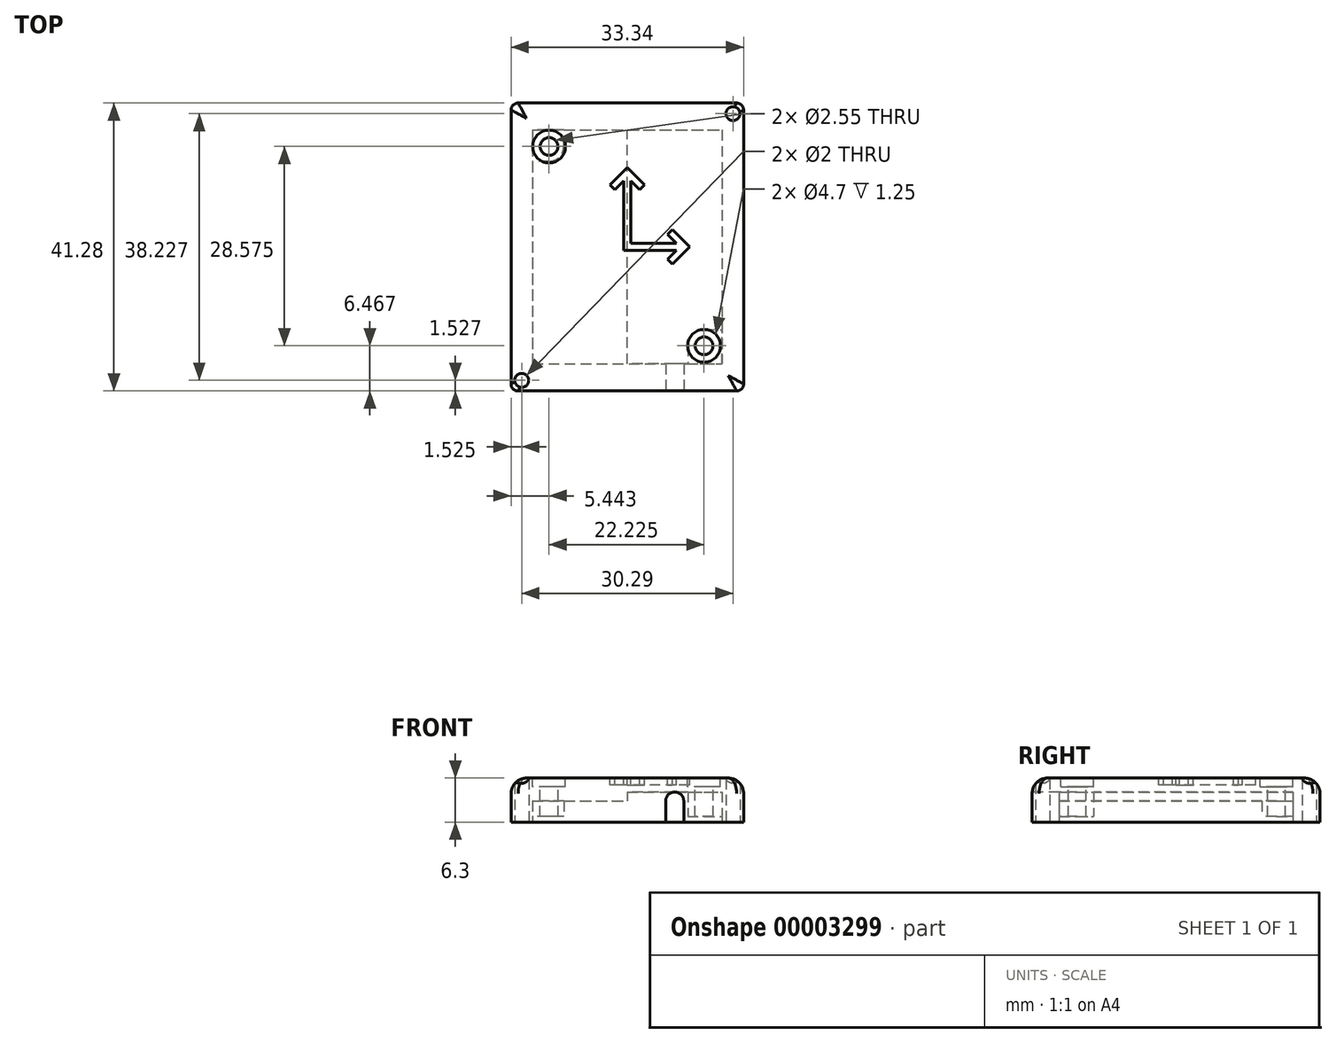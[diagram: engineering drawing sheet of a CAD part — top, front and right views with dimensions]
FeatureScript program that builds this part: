
annotation { "Feature Type Name" : "Feature", "Feature Type Description" : "" }
export const myFeature = defineFeature(function(context is Context, id is Id, definition is map)
    precondition{}
    {
        {
            var Q0;
            Q0=qCreatedBy(makeId("Top.planeOp"),FACE);
            var sketch = newSketch(context, id + "F0", { "sketchPlane" : qUnion([Q0])});
            skLineSegment(sketch, "E0.rect.bottom", {"start": v(16.67, 20.64) * mm, "end": v(-16.67, 20.64) * mm});
            skLineSegment(sketch, "E0.rect.top", {"start": v(16.67, -20.64) * mm, "end": v(-16.67, -20.64) * mm});
            skLineSegment(sketch, "E0.rect.left", {"start": v(16.67, 20.64) * mm, "end": v(16.67, -20.64) * mm});
            skLineSegment(sketch, "E0.rect.right", {"start": v(-16.67, 20.64) * mm, "end": v(-16.67, -20.64) * mm});
            skPoint(sketch, "E0.rect.middle", {"position": v(0, 0) * mm});
            skSolve(sketch);
        }
        {
            var Q0;
            Q0=qSketchRegion(id+"F0",true);
            extrude(context, id + "F1", {"entities" : qUnion([Q0]), "oppositeDirection" : true, "depth" : 5 * mm});
        }
        {
            var Q0;
            Q0=makeQuery(id+"F1.opExtrude","CAP_FACE",FACE,{"disambiguationData":[OSD([sQuery(id+"F0.wireOp",EDGE,"E0.rect.bottom"),sQuery(id+"F0.wireOp",EDGE,"E0.rect.top"),sQuery(id+"F0.wireOp",EDGE,"E0.rect.left"),sQuery(id+"F0.wireOp",EDGE,"E0.rect.right")])],"isStart":true});
            var sketch = newSketch(context, id + "F2", { "sketchPlane" : qUnion([Q0])});
            skLineSegment(sketch, "E1.rect.bottom", {"start": v(13.33, 16.51) * mm, "end": v(-13.34, 16.51) * mm});
            skLineSegment(sketch, "E1.rect.top", {"start": v(13.34, -16.51) * mm, "end": v(-13.33, -16.51) * mm});
            skLineSegment(sketch, "E1.rect.left", {"start": v(13.33, 16.51) * mm, "end": v(13.34, -16.51) * mm});
            skLineSegment(sketch, "E1.rect.right", {"start": v(-13.34, 16.51) * mm, "end": v(-13.33, -16.51) * mm});
            skPoint(sketch, "E1.rect.middle", {"position": v(0, 0) * mm});
            skCircle(sketch, "E2", {"center": v(11.23, 14.4) * mm, "radius": 1.25 * mm});
            skCircle(sketch, "E3", {"center": v(-11, -14.17) * mm, "radius": 1.25 * mm});
            skCircle(sketch, "E4", {"center": v(11.23, 14.4) * mm, "radius": 2.1 * mm});
            skCircle(sketch, "E5", {"center": v(-11, -14.17) * mm, "radius": 2.34 * mm});
            skLineSegment(sketch, "E6.0", {"start": v(13.59, 16.76) * mm, "end": v(-13.59, 16.76) * mm});
            skLineSegment(sketch, "E6.1", {"start": v(13.59, 16.76) * mm, "end": v(13.59, -16.76) * mm});
            skLineSegment(sketch, "E6.2", {"start": v(13.59, -16.76) * mm, "end": v(-13.59, -16.76) * mm});
            skLineSegment(sketch, "E6.3", {"start": v(-13.59, 16.76) * mm, "end": v(-13.59, -16.76) * mm});
            skLineSegment(sketch, "E7", {"start": v(9.12, 14.4) * mm, "end": v(9.12, 16.76) * mm});
            skLineSegment(sketch, "E8", {"start": v(11.23, 12.3) * mm, "end": v(13.59, 12.3) * mm});
            skLineSegment(sketch, "E9", {"start": v(-11, -11.84) * mm, "end": v(-13.59, -11.84) * mm});
            skLineSegment(sketch, "E10", {"start": v(-8.66, -14.17) * mm, "end": v(-8.66, -16.76) * mm});
            skSolve(sketch);
        }
        {
            var Q0;
            {var subQ6=sQuery(id+"F2.wireOp",EDGE,"E1.rect.right");var subQ10=sQuery(id+"F2.wireOp",EDGE,"E1.rect.bottom");var subQ18=makeQuery(id+"F2.imprint","INTERSECT",VERTEX,{"derivedFrom":[subQ10,subQ6]});Q0=makeQuery(id+"F2.imprint","IMPRINT",FACE,{"disambiguationData":[TD([[makeQuery(id+"F2.imprint","IMPRINT",EDGE,{"disambiguationData":[TD([[subQ18,1.0]])],"derivedFrom":subQ10}),1.0]])]});}
            var Q1;
            {var subQ1=sQuery(id+"F2.wireOp",EDGE,"E1.rect.right");var subQ6=sQuery(id+"F2.wireOp",EDGE,"E1.rect.bottom");var subQ11=makeQuery(id+"F2.imprint","INTERSECT",VERTEX,{"derivedFrom":[subQ6,subQ1]});Q1=makeQuery(id+"F2.imprint","IMPRINT",FACE,{"disambiguationData":[TD([[makeQuery(id+"F2.imprint","IMPRINT",EDGE,{"disambiguationData":[TD([[subQ11,1.0]])],"derivedFrom":subQ6}),-1.0]])]});}
            var Q2;
            {var subQ1=sQuery(id+"F2.wireOp",EDGE,"E1.rect.left");var subQ6=sQuery(id+"F2.wireOp",EDGE,"E1.rect.top");var subQ11=makeQuery(id+"F2.imprint","INTERSECT",VERTEX,{"derivedFrom":[subQ6,subQ1]});Q2=makeQuery(id+"F2.imprint","IMPRINT",FACE,{"disambiguationData":[TD([[makeQuery(id+"F2.imprint","IMPRINT",EDGE,{"disambiguationData":[TD([[subQ11,-1.0]])],"derivedFrom":subQ6}),1.0]])]});}
            extrude(context, id + "F3", {"entities" : qUnion([Q0, Q1, Q2]), "operationType" : NewBodyOperationType.REMOVE, "oppositeDirection" : true, "depth" : 3 * mm});
        }
        {
            var Q0;
            Q0=makeQuery(id+"F1.opExtrude","CAP_FACE",FACE,{"disambiguationData":[OSD([sQuery(id+"F0.wireOp",EDGE,"E0.rect.bottom"),sQuery(id+"F0.wireOp",EDGE,"E0.rect.top"),sQuery(id+"F0.wireOp",EDGE,"E0.rect.left"),sQuery(id+"F0.wireOp",EDGE,"E0.rect.right")])],"isStart":true});
            var sketch = newSketch(context, id + "F4", { "sketchPlane" : qUnion([Q0])});
            skLineSegment(sketch, "E11", {"start": v(9.12, 16.76) * mm, "end": v(13.59, 16.76) * mm});
            skLineSegment(sketch, "E12", {"start": v(13.59, 16.76) * mm, "end": v(13.59, 12.3) * mm});
            skLineSegment(sketch, "E13", {"start": v(13.59, 12.3) * mm, "end": v(11.23, 12.3) * mm});
            skArc(sketch, "E14", {"start": v(9.12, 14.4) * mm, "mid": v(9.74, 12.91) * mm, "end": v(11.23, 12.3) * mm});
            skLineSegment(sketch, "E15", {"start": v(9.12, 14.4) * mm, "end": v(9.12, 16.76) * mm});
            skArc(sketch, "E16", {"start": v(-8.66, -14.17) * mm, "mid": v(-9.35, -12.52) * mm, "end": v(-11, -11.84) * mm});
            skLineSegment(sketch, "E17", {"start": v(-8.66, -14.17) * mm, "end": v(-8.66, -16.76) * mm});
            skLineSegment(sketch, "E18", {"start": v(-8.66, -16.76) * mm, "end": v(-13.59, -16.76) * mm});
            skLineSegment(sketch, "E19", {"start": v(-13.59, -16.76) * mm, "end": v(-13.59, -11.84) * mm});
            skLineSegment(sketch, "E20", {"start": v(-13.59, -11.84) * mm, "end": v(-11, -11.84) * mm});
            skSolve(sketch);
        }
        {
            var Q0;
            Q0=qSketchRegion(id+"F4",true);
            extrude(context, id + "F5", {"entities" : qUnion([Q0]), "operationType" : NewBodyOperationType.REMOVE, "oppositeDirection" : true, "depth" : .8 * mm});
        }
        {
            var Q0;
            Q0=makeQuery(id+"F5.boolean.opBoolean","COPY",FACE,{"derivedFrom":makeQuery(id+"F5.opExtrude","CAP_FACE",FACE,{"disambiguationData":[OSD([sQuery(id+"F4.wireOp",EDGE,"E11"),sQuery(id+"F4.wireOp",EDGE,"E12"),sQuery(id+"F4.wireOp",EDGE,"E13"),sQuery(id+"F4.wireOp",EDGE,"E14"),sQuery(id+"F4.wireOp",EDGE,"E15")])],"isStart":false})});
            var sketch = newSketch(context, id + "F6", { "sketchPlane" : qUnion([Q0])});
            skCircle(sketch, "E21", {"center": v(11.23, 14.4) * mm, "radius": 1.02 * mm});
            skSolve(sketch);
        }
        {
            var Q0;
            Q0=qSketchRegion(id+"F6",true);
            extrude(context, id + "F7", {"entities" : qUnion([Q0]), "operationType" : NewBodyOperationType.REMOVE, "oppositeDirection" : true, "depth" : 25.4 * mm});
        }
        {
            var Q0;
            Q0=makeQuery(id+"F5.boolean.opBoolean","COPY",FACE,{"derivedFrom":makeQuery(id+"F5.opExtrude","CAP_FACE",FACE,{"disambiguationData":[OSD([sQuery(id+"F4.wireOp",EDGE,"E16"),sQuery(id+"F4.wireOp",EDGE,"E17"),sQuery(id+"F4.wireOp",EDGE,"E18"),sQuery(id+"F4.wireOp",EDGE,"E19"),sQuery(id+"F4.wireOp",EDGE,"E20")])],"isStart":false})});
            var sketch = newSketch(context, id + "F8", { "sketchPlane" : qUnion([Q0])});
            skCircle(sketch, "E22", {"center": v(-11, -14.17) * mm, "radius": 1.02 * mm});
            skSolve(sketch);
        }
        {
            var Q0;
            Q0=qSketchRegion(id+"F8",true);
            extrude(context, id + "F9", {"entities" : qUnion([Q0]), "operationType" : NewBodyOperationType.REMOVE, "oppositeDirection" : true, "depth" : 25.4 * mm});
        }
        {
            var Q0;
            Q0=makeQuery(id+"F1.opExtrude","CAP_FACE",FACE,{"disambiguationData":[OSD([sQuery(id+"F0.wireOp",EDGE,"E0.rect.bottom"),sQuery(id+"F0.wireOp",EDGE,"E0.rect.top"),sQuery(id+"F0.wireOp",EDGE,"E0.rect.left"),sQuery(id+"F0.wireOp",EDGE,"E0.rect.right")])],"isStart":true});
            var sketch = newSketch(context, id + "F10", { "sketchPlane" : qUnion([Q0])});
            skLineSegment(sketch, "E23.bottom", {"start": v(-13.59, 16.76) * mm, "end": v(-5.09, 16.76) * mm});
            skLineSegment(sketch, "E23.top", {"start": v(-13.59, 20.64) * mm, "end": v(-5.09, 20.64) * mm});
            skLineSegment(sketch, "E23.left", {"start": v(-13.59, 16.76) * mm, "end": v(-13.59, 20.64) * mm});
            skLineSegment(sketch, "E23.right", {"start": v(-5.09, 16.76) * mm, "end": v(-5.09, 20.64) * mm});
            skLineSegment(sketch, "E24.bottom", {"start": v(13.59, -16.76) * mm, "end": v(4.59, -16.76) * mm});
            skLineSegment(sketch, "E24.top", {"start": v(13.59, -20.64) * mm, "end": v(4.59, -20.64) * mm});
            skLineSegment(sketch, "E24.left", {"start": v(13.59, -16.76) * mm, "end": v(13.59, -20.64) * mm});
            skLineSegment(sketch, "E24.right", {"start": v(4.59, -16.76) * mm, "end": v(4.59, -20.64) * mm});
            skSolve(sketch);
        }
        {
            var Q0;
            Q0=qSketchRegion(id+"F10",true);
            extrude(context, id + "F11", {"entities" : qUnion([Q0]), "operationType" : NewBodyOperationType.REMOVE, "oppositeDirection" : true, "depth" : .4 * mm});
        }
        {
            var Q0;
            {var subQ0=sQuery(id+"F0.wireOp",EDGE,"E0.rect.bottom");var subQ1=sQuery(id+"F0.wireOp",EDGE,"E0.rect.top");var subQ2=sQuery(id+"F0.wireOp",EDGE,"E0.rect.right");Q0=makeQuery(id+"F11.boolean.opBoolean","SPLIT",FACE,{"disambiguationData":[TD([makeQuery(id+"F1.opExtrude","SWEPT_FACE",FACE,{"disambiguationData":[OSD([subQ2])]})])],"derivedFrom":makeQuery(id+"F1.opExtrude","CAP_FACE",FACE,{"disambiguationData":[OSD([subQ0,subQ1,sQuery(id+"F0.wireOp",EDGE,"E0.rect.left"),subQ2])],"isStart":true})});}
            var sketch = newSketch(context, id + "F12", { "sketchPlane" : qUnion([Q0])});
            skCircle(sketch, "E25", {"center": v(-15.14, 19.11) * mm, "radius": 1 * mm});
            skSolve(sketch);
        }
        {
            var Q0;
            Q0=qSketchRegion(id+"F12",true);
            extrude(context, id + "F13", {"entities" : qUnion([Q0]), "operationType" : NewBodyOperationType.ADD, "depth" : 3.5 * mm});
        }
        {
            var Q0;
            {var subQ0=sQuery(id+"F0.wireOp",EDGE,"E0.rect.bottom");var subQ1=sQuery(id+"F0.wireOp",EDGE,"E0.rect.top");var subQ2=sQuery(id+"F0.wireOp",EDGE,"E0.rect.left");Q0=makeQuery(id+"F11.boolean.opBoolean","SPLIT",FACE,{"disambiguationData":[TD([makeQuery(id+"F1.opExtrude","SWEPT_FACE",FACE,{"disambiguationData":[OSD([subQ2])]})])],"derivedFrom":makeQuery(id+"F1.opExtrude","CAP_FACE",FACE,{"disambiguationData":[OSD([subQ0,subQ1,subQ2,sQuery(id+"F0.wireOp",EDGE,"E0.rect.right")])],"isStart":true})});}
            var sketch = newSketch(context, id + "F14", { "sketchPlane" : qUnion([Q0])});
            skCircle(sketch, "E26", {"center": v(15.14, -19.11) * mm, "radius": 1 * mm});
            skSolve(sketch);
        }
        {
            var Q0;
            Q0=qSketchRegion(id+"F14",true);
            extrude(context, id + "F15", {"entities" : qUnion([Q0]), "operationType" : NewBodyOperationType.ADD, "depth" : 3.5 * mm});
        }
        {
            var Q0;
            Q0=makeQuery(id+"F13.opExtrude","CAP_EDGE",EDGE,{"disambiguationData":[OSD([sQuery(id+"F12.wireOp",EDGE,"E25")])],"isStart":false});
            var Q1;
            Q1=makeQuery(id+"F15.opExtrude","CAP_EDGE",EDGE,{"disambiguationData":[OSD([sQuery(id+"F14.wireOp",EDGE,"E26")])],"isStart":false});
            fillet(context, id + "F16", {"entities" : qUnion([Q0, Q1]), "radius" : 1 * mm, "tangentPropagation" : true, "allowEdgeOverflow" : false});
        }
        {
            var Q0;
            Q0=makeQuery(id+"F1.opExtrude","SWEPT_EDGE",EDGE,{"disambiguationData":[OSD([sQuery(id+"F0.wireOp",EDGE,"E0.rect.bottom"),sQuery(id+"F0.wireOp",EDGE,"E0.rect.left")])]});
            var Q1;
            Q1=makeQuery(id+"F1.opExtrude","SWEPT_EDGE",EDGE,{"disambiguationData":[OSD([sQuery(id+"F0.wireOp",EDGE,"E0.rect.top"),sQuery(id+"F0.wireOp",EDGE,"E0.rect.left")])]});
            var Q2;
            Q2=makeQuery(id+"F1.opExtrude","SWEPT_EDGE",EDGE,{"disambiguationData":[OSD([sQuery(id+"F0.wireOp",EDGE,"E0.rect.top"),sQuery(id+"F0.wireOp",EDGE,"E0.rect.right")])]});
            var Q3;
            Q3=makeQuery(id+"F1.opExtrude","SWEPT_EDGE",EDGE,{"disambiguationData":[OSD([sQuery(id+"F0.wireOp",EDGE,"E0.rect.bottom"),sQuery(id+"F0.wireOp",EDGE,"E0.rect.right")])]});
            var Q4;
            Q4=makeQuery(id+"F1.opExtrude","CAP_EDGE",EDGE,{"disambiguationData":[OSD([sQuery(id+"F0.wireOp",EDGE,"E0.rect.top")])],"isStart":false});
            var Q5;
            Q5=makeQuery(id+"F1.opExtrude","CAP_EDGE",EDGE,{"disambiguationData":[OSD([sQuery(id+"F0.wireOp",EDGE,"E0.rect.left")])],"isStart":false});
            var Q6;
            Q6=makeQuery(id+"F1.opExtrude","CAP_EDGE",EDGE,{"disambiguationData":[OSD([sQuery(id+"F0.wireOp",EDGE,"E0.rect.bottom")])],"isStart":false});
            var Q7;
            Q7=makeQuery(id+"F1.opExtrude","CAP_EDGE",EDGE,{"disambiguationData":[OSD([sQuery(id+"F0.wireOp",EDGE,"E0.rect.right")])],"isStart":false});
            fillet(context, id + "F17", {"entities" : qUnion([Q0, Q1, Q2, Q3, Q4, Q5, Q6, Q7]), "radius" : 1 * mm, "tangentPropagation" : true, "allowEdgeOverflow" : false});
        }
        {
            var Q0;
            Q0=makeQuery(id+"F11.boolean.opBoolean","COPY",FACE,{"derivedFrom":makeQuery(id+"F11.opExtrude","CAP_FACE",FACE,{"disambiguationData":[OSD([sQuery(id+"F10.wireOp",EDGE,"E24.bottom"),sQuery(id+"F10.wireOp",EDGE,"E24.top"),sQuery(id+"F10.wireOp",EDGE,"E24.left"),sQuery(id+"F10.wireOp",EDGE,"E24.right")])],"isStart":false})});
            var sketch = newSketch(context, id + "F18", { "sketchPlane" : qUnion([Q0])});
            skLineSegment(sketch, "E27.bottom", {"start": v(4.59, -16.76) * mm, "end": v(13.59, -16.76) * mm});
            skLineSegment(sketch, "E27.top", {"start": v(4.59, -20.64) * mm, "end": v(13.59, -20.64) * mm});
            skLineSegment(sketch, "E27.left", {"start": v(4.59, -16.76) * mm, "end": v(4.59, -20.64) * mm});
            skLineSegment(sketch, "E27.right", {"start": v(13.59, -16.76) * mm, "end": v(13.59, -20.64) * mm});
            skSolve(sketch);
        }
        {
            var Q0;
            Q0=qSketchRegion(id+"F18",true);
            extrude(context, id + "F19", {"entities" : qUnion([Q0]), "operationType" : NewBodyOperationType.ADD, "depth" : .4 * mm});
        }
        {
            var Q0;
            Q0=makeQuery(id+"F11.boolean.opBoolean","COPY",FACE,{"derivedFrom":makeQuery(id+"F11.opExtrude","CAP_FACE",FACE,{"disambiguationData":[OSD([sQuery(id+"F10.wireOp",EDGE,"E23.bottom"),sQuery(id+"F10.wireOp",EDGE,"E23.top"),sQuery(id+"F10.wireOp",EDGE,"E23.left"),sQuery(id+"F10.wireOp",EDGE,"E23.right")])],"isStart":false})});
            var sketch = newSketch(context, id + "F20", { "sketchPlane" : qUnion([Q0])});
            skLineSegment(sketch, "E28.bottom", {"start": v(-13.59, 20.64) * mm, "end": v(-5.09, 20.64) * mm});
            skLineSegment(sketch, "E28.top", {"start": v(-13.59, 16.76) * mm, "end": v(-5.09, 16.76) * mm});
            skLineSegment(sketch, "E28.left", {"start": v(-13.59, 20.64) * mm, "end": v(-13.59, 16.76) * mm});
            skLineSegment(sketch, "E28.right", {"start": v(-5.09, 20.64) * mm, "end": v(-5.09, 16.76) * mm});
            skSolve(sketch);
        }
        {
            var Q0;
            Q0=qSketchRegion(id+"F20",true);
            extrude(context, id + "F21", {"entities" : qUnion([Q0]), "operationType" : NewBodyOperationType.ADD, "depth" : .4 * mm});
        }
        {
            var Q0;
            Q0=qCreatedBy(makeId("Top.planeOp"),FACE);
            var sketch = newSketch(context, id + "F22", { "sketchPlane" : qUnion([Q0])});
            skLineSegment(sketch, "E29", {"start": v(0, 0) * mm, "end": v(0, 40.72) * mm});
            skSolve(sketch);
        }
        {
            var Q0;
            Q0=makeQuery(id+"F1.opExtrude","SWEPT_BODY",BODY,{"disambiguationData":[OSD([sQuery(id+"F0.wireOp",EDGE,"E0.rect.bottom"),sQuery(id+"F0.wireOp",EDGE,"E0.rect.top"),sQuery(id+"F0.wireOp",EDGE,"E0.rect.left"),sQuery(id+"F0.wireOp",EDGE,"E0.rect.right")])]});
            var Q1;
            Q1=sQuery(id+"F22.wireOp",EDGE,"E29");
            transform(context, id + "F23", {"entities" : qUnion([Q0]), "transformType" : TransformType.ROTATION, "transformAxis" : qUnion([Q1]), "angle" : 180 * degree, "makeCopy" : false});
        }
        {
            var Q0;
            Q0=makeQuery(id+"F1.opExtrude","SWEPT_BODY",BODY,{"disambiguationData":[OSD([sQuery(id+"F0.wireOp",EDGE,"E0.rect.bottom"),sQuery(id+"F0.wireOp",EDGE,"E0.rect.top"),sQuery(id+"F0.wireOp",EDGE,"E0.rect.left"),sQuery(id+"F0.wireOp",EDGE,"E0.rect.right")])]});
            var Q1;
            Q1=qCreatedBy(makeId("Top.planeOp"),FACE);
            mirror(context, id + "F24", {"entities" : qUnion([Q0]), "mirrorPlane" : qUnion([Q1])});
        }
        {
            var Q0;
            Q0=makeQuery(id+"F1.opExtrude","SWEPT_BODY",BODY,{"disambiguationData":[OSD([sQuery(id+"F0.wireOp",EDGE,"E0.rect.bottom"),sQuery(id+"F0.wireOp",EDGE,"E0.rect.top"),sQuery(id+"F0.wireOp",EDGE,"E0.rect.left"),sQuery(id+"F0.wireOp",EDGE,"E0.rect.right")])]});
            deleteBodies(context, id + "F25", {"entities" : qUnion([Q0])});
        }
        {
            var Q0;
            Q0=makeQuery(id+"F24.opPattern","COPY",BODY,{"derivedFrom":makeQuery(id+"F1.opExtrude","SWEPT_BODY",BODY,{"disambiguationData":[OSD([sQuery(id+"F0.wireOp",EDGE,"E0.rect.bottom"),sQuery(id+"F0.wireOp",EDGE,"E0.rect.top"),sQuery(id+"F0.wireOp",EDGE,"E0.rect.left"),sQuery(id+"F0.wireOp",EDGE,"E0.rect.right")])]}),"instanceName":"1"});
            var Q1;
            Q1=qCreatedBy(makeId("Top.planeOp"),FACE);
            mirror(context, id + "F26", {"entities" : qUnion([Q0]), "mirrorPlane" : qUnion([Q1])});
        }
        {
            var Q0;
            Q0=makeQuery(id+"F24.opPattern","COPY",BODY,{"derivedFrom":makeQuery(id+"F1.opExtrude","SWEPT_BODY",BODY,{"disambiguationData":[OSD([sQuery(id+"F0.wireOp",EDGE,"E0.rect.bottom"),sQuery(id+"F0.wireOp",EDGE,"E0.rect.top"),sQuery(id+"F0.wireOp",EDGE,"E0.rect.left"),sQuery(id+"F0.wireOp",EDGE,"E0.rect.right")])]}),"instanceName":"1"});
            deleteBodies(context, id + "F27", {"entities" : qUnion([Q0])});
        }
        {
            var Q0;
            {var subQ0=sQuery(id+"F0.wireOp",EDGE,"E0.rect.bottom");var subQ1=sQuery(id+"F0.wireOp",EDGE,"E0.rect.top");var subQ2=sQuery(id+"F0.wireOp",EDGE,"E0.rect.left");var subQ3=sQuery(id+"F0.wireOp",EDGE,"E0.rect.right");var subQ4=makeQuery(id+"F1.opExtrude","CAP_FACE",FACE,{"disambiguationData":[OSD([subQ0,subQ1,subQ2,subQ3])],"isStart":true});Q0=makeQuery(id+"F26.opPattern","COPY",FACE,{"derivedFrom":makeQuery(id+"F24.opPattern","COPY",FACE,{"derivedFrom":makeQuery(id+"F21.boolean.opBoolean","MERGE",FACE,{"derivedFrom":[makeQuery(id+"F19.boolean.opBoolean","MERGE",FACE,{"derivedFrom":[makeQuery(id+"F11.boolean.opBoolean","SPLIT",FACE,{"disambiguationData":[TD([makeQuery(id+"F1.opExtrude","SWEPT_FACE",FACE,{"disambiguationData":[OSD([subQ3])]})])],"derivedFrom":subQ4}),makeQuery(id+"F11.boolean.opBoolean","SPLIT",FACE,{"disambiguationData":[TD([makeQuery(id+"F1.opExtrude","SWEPT_FACE",FACE,{"disambiguationData":[OSD([subQ2])]})])],"derivedFrom":subQ4}),makeQuery(id+"F19.opExtrude","CAP_FACE",FACE,{"disambiguationData":[OSD([sQuery(id+"F18.wireOp",EDGE,"E27.bottom"),sQuery(id+"F18.wireOp",EDGE,"E27.top"),sQuery(id+"F18.wireOp",EDGE,"E27.left"),sQuery(id+"F18.wireOp",EDGE,"E27.right")])],"isStart":false})]}),makeQuery(id+"F21.opExtrude","CAP_FACE",FACE,{"disambiguationData":[OSD([sQuery(id+"F20.wireOp",EDGE,"E28.bottom"),sQuery(id+"F20.wireOp",EDGE,"E28.top"),sQuery(id+"F20.wireOp",EDGE,"E28.left"),sQuery(id+"F20.wireOp",EDGE,"E28.right")])],"isStart":false})]}),"instanceName":"1"}),"instanceName":"1"});}
            var sketch = newSketch(context, id + "F28", { "sketchPlane" : qUnion([Q0])});
            skCircle(sketch, "E30", {"center": v(-15.14, 19.11) * mm, "radius": 1 * mm});
            skPoint(sketch, "E30.first.point", {"position": v(-15.31, 18.13) * mm});
            skPoint(sketch, "E30.second.point", {"position": v(-14.3, 19.64) * mm});
            skPoint(sketch, "E30.third.point", {"position": v(-15.62, 20) * mm});
            skCircle(sketch, "E31", {"center": v(15.14, -19.11) * mm, "radius": 1 * mm});
            skPoint(sketch, "E31.first.point", {"position": v(15.27, -18.12) * mm});
            skPoint(sketch, "E31.second.point", {"position": v(14.16, -19.27) * mm});
            skPoint(sketch, "E31.third.point", {"position": v(15.62, -20) * mm});
            skSolve(sketch);
        }
        {
            var Q0;
            Q0 = qSketchRegion(id + "F28", true);
            extrude(context, id + "F29", {"entities" : qUnion([Q0]), "operationType" : NewBodyOperationType.REMOVE, "endBound" : BoundingType.SYMMETRIC, "oppositeDirection" : true, "depth" : 25.4 * mm});
        }
        {
            var Q0;
            Q0=makeQuery(id+"F26.opPattern","COPY",FACE,{"derivedFrom":makeQuery(id+"F24.opPattern","COPY",FACE,{"derivedFrom":makeQuery(id+"F3.boolean.opBoolean","COPY",FACE,{"derivedFrom":makeQuery(id+"F3.opExtrude","CAP_FACE",FACE,{"disambiguationData":[OSD([sQuery(id+"F2.wireOp",EDGE,"E4"),sQuery(id+"F2.wireOp",EDGE,"E5"),sQuery(id+"F2.wireOp",EDGE,"E6.0"),sQuery(id+"F2.wireOp",EDGE,"E6.1"),sQuery(id+"F2.wireOp",EDGE,"E6.2"),sQuery(id+"F2.wireOp",EDGE,"E6.3"),sQuery(id+"F2.wireOp",EDGE,"E7"),sQuery(id+"F2.wireOp",EDGE,"E8"),sQuery(id+"F2.wireOp",EDGE,"E9"),sQuery(id+"F2.wireOp",EDGE,"E10")])],"isStart":false})}),"instanceName":"1"}),"instanceName":"1"});
            var sketch = newSketch(context, id + "F30", { "sketchPlane" : qUnion([Q0])});
            skLineSegment(sketch, "E32.rect.bottom", {"start": v(-16.67, 20.64) * mm, "end": v(16.67, 20.64) * mm});
            skLineSegment(sketch, "E32.rect.top", {"start": v(-16.67, -20.64) * mm, "end": v(16.67, -20.64) * mm});
            skLineSegment(sketch, "E32.rect.left", {"start": v(-16.67, 20.64) * mm, "end": v(-16.67, -20.64) * mm});
            skLineSegment(sketch, "E32.rect.right", {"start": v(16.67, 20.64) * mm, "end": v(16.67, -20.64) * mm});
            skPoint(sketch, "E32.rect.middle", {"position": v(0, 0) * mm});
            skCircle(sketch, "E33", {"center": v(-15.14, 19.11) * mm, "radius": 1 * mm});
            skPoint(sketch, "E33.first.point", {"position": v(-15.8, 18.35) * mm});
            skPoint(sketch, "E33.second.point", {"position": v(-16.07, 19.48) * mm});
            skPoint(sketch, "E33.third.point", {"position": v(-14.93, 20.1) * mm});
            skCircle(sketch, "E34", {"center": v(11, 14.17) * mm, "radius": 1.02 * mm});
            skCircle(sketch, "E35", {"center": v(-11.23, -14.4) * mm, "radius": 1.02 * mm});
            skCircle(sketch, "E36", {"center": v(15.14, -19.11) * mm, "radius": 1 * mm});
            skPoint(sketch, "E36.first.point", {"position": v(14.52, -19.9) * mm});
            skPoint(sketch, "E36.second.point", {"position": v(14.45, -18.4) * mm});
            skPoint(sketch, "E36.third.point", {"position": v(15.29, -18.12) * mm});
            skSolve(sketch);
        }
        {
            var Q0;
            Q0 = qSketchRegion(id + "F30", true);
            extrude(context, id + "F31", {"entities" : qUnion([Q0]), "operationType" : NewBodyOperationType.ADD, "oppositeDirection" : true, "depth" : 3.3 * mm});
        }
        {
            var Q0;
            {var subQ0=sQuery(id+"F0.wireOp",EDGE,"E0.rect.bottom");var subQ1=sQuery(id+"F0.wireOp",EDGE,"E0.rect.top");var subQ2=sQuery(id+"F0.wireOp",EDGE,"E0.rect.left");var subQ3=sQuery(id+"F0.wireOp",EDGE,"E0.rect.right");var subQ4=makeQuery(id+"F1.opExtrude","CAP_FACE",FACE,{"disambiguationData":[OSD([subQ0,subQ1,subQ2,subQ3])],"isStart":true});Q0=makeQuery(id+"F26.opPattern","COPY",FACE,{"derivedFrom":makeQuery(id+"F24.opPattern","COPY",FACE,{"derivedFrom":makeQuery(id+"F21.boolean.opBoolean","MERGE",FACE,{"derivedFrom":[makeQuery(id+"F19.boolean.opBoolean","MERGE",FACE,{"derivedFrom":[makeQuery(id+"F11.boolean.opBoolean","SPLIT",FACE,{"disambiguationData":[TD([makeQuery(id+"F1.opExtrude","SWEPT_FACE",FACE,{"disambiguationData":[OSD([subQ3])]})])],"derivedFrom":subQ4}),makeQuery(id+"F11.boolean.opBoolean","SPLIT",FACE,{"disambiguationData":[TD([makeQuery(id+"F1.opExtrude","SWEPT_FACE",FACE,{"disambiguationData":[OSD([subQ2])]})])],"derivedFrom":subQ4}),makeQuery(id+"F19.opExtrude","CAP_FACE",FACE,{"disambiguationData":[OSD([sQuery(id+"F18.wireOp",EDGE,"E27.bottom"),sQuery(id+"F18.wireOp",EDGE,"E27.top"),sQuery(id+"F18.wireOp",EDGE,"E27.left"),sQuery(id+"F18.wireOp",EDGE,"E27.right")])],"isStart":false})]}),makeQuery(id+"F21.opExtrude","CAP_FACE",FACE,{"disambiguationData":[OSD([sQuery(id+"F20.wireOp",EDGE,"E28.bottom"),sQuery(id+"F20.wireOp",EDGE,"E28.top"),sQuery(id+"F20.wireOp",EDGE,"E28.left"),sQuery(id+"F20.wireOp",EDGE,"E28.right")])],"isStart":false})]}),"instanceName":"1"}),"instanceName":"1"});}
            var sketch = newSketch(context, id + "F32", { "sketchPlane" : qUnion([Q0])});
            skLineSegment(sketch, "E37.bottom", {"start": v(5.49, 16.76) * mm, "end": v(8.09, 16.76) * mm});
            skLineSegment(sketch, "E37.top", {"start": v(5.49, 20.64) * mm, "end": v(8.09, 20.64) * mm});
            skLineSegment(sketch, "E37.left", {"start": v(5.49, 16.76) * mm, "end": v(5.49, 20.64) * mm});
            skLineSegment(sketch, "E37.right", {"start": v(8.09, 16.76) * mm, "end": v(8.09, 20.64) * mm});
            skSolve(sketch);
        }
        {
            var Q0;
            Q0 = qSketchRegion(id + "F32", true);
            extrude(context, id + "F33", {"entities" : qUnion([Q0]), "operationType" : NewBodyOperationType.REMOVE, "oppositeDirection" : true, "depth" : 3 * mm});
        }
        {
            var Q0;
            Q0=makeQuery(id+"F31.boolean.opBoolean","MERGE",FACE,{"derivedFrom":[makeQuery(id+"F26.opPattern","COPY",FACE,{"derivedFrom":makeQuery(id+"F24.opPattern","COPY",FACE,{"derivedFrom":makeQuery(id+"F19.boolean.opBoolean","MERGE",FACE,{"derivedFrom":[makeQuery(id+"F1.opExtrude","SWEPT_FACE",FACE,{"disambiguationData":[OSD([sQuery(id+"F0.wireOp",EDGE,"E0.rect.top")])]}),makeQuery(id+"F19.opExtrude","SWEPT_FACE",FACE,{"disambiguationData":[OSD([sQuery(id+"F18.wireOp",EDGE,"E27.top")])]})]}),"instanceName":"1"}),"instanceName":"1"}),makeQuery(id+"F31.opExtrude","SWEPT_FACE",FACE,{"disambiguationData":[OSD([sQuery(id+"F30.wireOp",EDGE,"E32.rect.bottom")])]})]});
            var sketch = newSketch(context, id + "F34", { "sketchPlane" : qUnion([Q0])});
            skCircle(sketch, "E38", {"center": v(6.79, 3) * mm, "radius": 1.3 * mm});
            skSolve(sketch);
        }
        {
            var Q0;
            Q0 = qSketchRegion(id + "F34", true);
            extrude(context, id + "F35", {"entities" : qUnion([Q0]), "operationType" : NewBodyOperationType.REMOVE, "oppositeDirection" : true, "depth" : 4 * mm});
        }
        {
            var Q0;
            Q0=makeQuery(id+"F33.boolean.opBoolean","MERGE",FACE,{"derivedFrom":[makeQuery(id+"F26.opPattern","COPY",FACE,{"derivedFrom":makeQuery(id+"F24.opPattern","COPY",FACE,{"derivedFrom":makeQuery(id+"F3.boolean.opBoolean","COPY",FACE,{"derivedFrom":makeQuery(id+"F3.opExtrude","CAP_FACE",FACE,{"disambiguationData":[OSD([sQuery(id+"F2.wireOp",EDGE,"E4"),sQuery(id+"F2.wireOp",EDGE,"E5"),sQuery(id+"F2.wireOp",EDGE,"E6.0"),sQuery(id+"F2.wireOp",EDGE,"E6.1"),sQuery(id+"F2.wireOp",EDGE,"E6.2"),sQuery(id+"F2.wireOp",EDGE,"E6.3"),sQuery(id+"F2.wireOp",EDGE,"E7"),sQuery(id+"F2.wireOp",EDGE,"E8"),sQuery(id+"F2.wireOp",EDGE,"E9"),sQuery(id+"F2.wireOp",EDGE,"E10")])],"isStart":false})}),"instanceName":"1"}),"instanceName":"1"}),makeQuery(id+"F33.opExtrude","CAP_FACE",FACE,{"disambiguationData":[OSD([sQuery(id+"F32.wireOp",EDGE,"E37.bottom"),sQuery(id+"F32.wireOp",EDGE,"E37.top"),sQuery(id+"F32.wireOp",EDGE,"E37.left"),sQuery(id+"F32.wireOp",EDGE,"E37.right")])],"isStart":false})]});
            var sketch = newSketch(context, id + "F36", { "sketchPlane" : qUnion([Q0])});
            skLineSegment(sketch, "E39", {"start": v(0, 16.76) * mm, "end": v(0, -16.76) * mm});
            skLineSegment(sketch, "E40", {"start": v(0, -16.76) * mm, "end": v(13.59, -16.76) * mm});
            skLineSegment(sketch, "E41", {"start": v(13.59, -16.76) * mm, "end": v(13.59, 11.84) * mm});
            skLineSegment(sketch, "E42", {"start": v(13.59, 11.84) * mm, "end": v(11, 11.84) * mm});
            skArc(sketch, "E43", {"start": v(8.66, 14.17) * mm, "mid": v(9.35, 12.52) * mm, "end": v(11, 11.84) * mm});
            skLineSegment(sketch, "E44", {"start": v(8.66, 14.17) * mm, "end": v(8.66, 16.76) * mm});
            skLineSegment(sketch, "E45", {"start": v(8.66, 16.76) * mm, "end": v(0, 16.76) * mm});
            skSolve(sketch);
        }
        {
            var Q0;
            Q0 = qSketchRegion(id + "F36", true);
            extrude(context, id + "F37", {"entities" : qUnion([Q0]), "operationType" : NewBodyOperationType.REMOVE, "oppositeDirection" : true, "depth" : 1.3 * mm});
        }
        {
            var Q0;
            Q0=makeQuery(id+"F31.opExtrude","SWEPT_EDGE",EDGE,{"disambiguationData":[OSD([sQuery(id+"F30.wireOp",EDGE,"E32.rect.bottom"),sQuery(id+"F30.wireOp",EDGE,"E32.rect.right")])]});
            var Q1;
            Q1=makeQuery(id+"F31.opExtrude","SWEPT_EDGE",EDGE,{"disambiguationData":[OSD([sQuery(id+"F30.wireOp",EDGE,"E32.rect.bottom"),sQuery(id+"F30.wireOp",EDGE,"E32.rect.left")])]});
            var Q2;
            Q2=makeQuery(id+"F31.opExtrude","SWEPT_EDGE",EDGE,{"disambiguationData":[OSD([sQuery(id+"F30.wireOp",EDGE,"E32.rect.top"),sQuery(id+"F30.wireOp",EDGE,"E32.rect.right")])]});
            var Q3;
            Q3=makeQuery(id+"F31.opExtrude","SWEPT_EDGE",EDGE,{"disambiguationData":[OSD([sQuery(id+"F30.wireOp",EDGE,"E32.rect.top"),sQuery(id+"F30.wireOp",EDGE,"E32.rect.left")])]});
            fillet(context, id + "F38", {"entities" : qUnion([Q0, Q1, Q2, Q3]), "radius" : 1 * mm, "tangentPropagation" : true, "allowEdgeOverflow" : false});
        }
        {
            var Q0;
            Q0=makeQuery(id+"F31.opExtrude","CAP_EDGE",EDGE,{"disambiguationData":[OSD([sQuery(id+"F30.wireOp",EDGE,"E32.rect.right")])],"isStart":false});
            fillet(context, id + "F39", {"entities" : qUnion([Q0]), "radius" : 2.2 * mm, "tangentPropagation" : true, "allowEdgeOverflow" : false});
        }
        {
            var Q0;
            Q0=makeQuery(id+"F31.opExtrude","CAP_FACE",FACE,{"disambiguationData":[OSD([sQuery(id+"F30.wireOp",EDGE,"E32.rect.bottom"),sQuery(id+"F30.wireOp",EDGE,"E32.rect.top"),sQuery(id+"F30.wireOp",EDGE,"E32.rect.left"),sQuery(id+"F30.wireOp",EDGE,"E32.rect.right"),sQuery(id+"F30.wireOp",EDGE,"E33"),sQuery(id+"F30.wireOp",EDGE,"E34"),sQuery(id+"F30.wireOp",EDGE,"E35"),sQuery(id+"F30.wireOp",EDGE,"E36")])],"isStart":false});
            var sketch = newSketch(context, id + "F40", { "sketchPlane" : qUnion([Q0])});
            skCircle(sketch, "E46", {"center": v(-11.23, 14.4) * mm, "radius": 1.27 * mm});
            skCircle(sketch, "E47", {"center": v(11, -14.17) * mm, "radius": 1.27 * mm});
            skSolve(sketch);
        }
        {
            var Q0;
            Q0 = qSketchRegion(id + "F40", true);
            extrude(context, id + "F41", {"entities" : qUnion([Q0]), "operationType" : NewBodyOperationType.REMOVE, "oppositeDirection" : true, "depth" : 25 * mm});
        }
        {
            var Q0;
            Q0=makeQuery(id+"F31.opExtrude","CAP_FACE",FACE,{"disambiguationData":[OSD([sQuery(id+"F30.wireOp",EDGE,"E32.rect.bottom"),sQuery(id+"F30.wireOp",EDGE,"E32.rect.top"),sQuery(id+"F30.wireOp",EDGE,"E32.rect.left"),sQuery(id+"F30.wireOp",EDGE,"E32.rect.right"),sQuery(id+"F30.wireOp",EDGE,"E33"),sQuery(id+"F30.wireOp",EDGE,"E34"),sQuery(id+"F30.wireOp",EDGE,"E35"),sQuery(id+"F30.wireOp",EDGE,"E36")])],"isStart":false});
            var sketch = newSketch(context, id + "F42", { "sketchPlane" : qUnion([Q0])});
            skCircle(sketch, "E48", {"center": v(-11.23, 14.4) * mm, "radius": 2.35 * mm});
            skCircle(sketch, "E49", {"center": v(11, -14.17) * mm, "radius": 2.35 * mm});
            skSolve(sketch);
        }
        {
            var Q0;
            Q0 = qSketchRegion(id + "F42", true);
            extrude(context, id + "F43", {"entities" : qUnion([Q0]), "operationType" : NewBodyOperationType.REMOVE, "oppositeDirection" : true, "depth" : 1.25 * mm});
        }
        {
            var Q0;
            Q0=makeQuery(id+"F31.opExtrude","CAP_FACE",FACE,{"disambiguationData":[OSD([sQuery(id+"F30.wireOp",EDGE,"E32.rect.bottom"),sQuery(id+"F30.wireOp",EDGE,"E32.rect.top"),sQuery(id+"F30.wireOp",EDGE,"E32.rect.left"),sQuery(id+"F30.wireOp",EDGE,"E32.rect.right"),sQuery(id+"F30.wireOp",EDGE,"E33"),sQuery(id+"F30.wireOp",EDGE,"E34"),sQuery(id+"F30.wireOp",EDGE,"E35"),sQuery(id+"F30.wireOp",EDGE,"E36")])],"isStart":false});
            var sketch = newSketch(context, id + "F44", { "sketchPlane" : qUnion([Q0])});
            skLineSegment(sketch, "E50.rect.bottom", {"start": v(-0.5, 10) * mm, "end": v(0.5, 10) * mm});
            skLineSegment(sketch, "E50.rect.top", {"start": v(-0.5, -10) * mm, "end": v(0.5, -10) * mm});
            skLineSegment(sketch, "E50.rect.left", {"start": v(-0.5, 10) * mm, "end": v(-0.5, -10) * mm});
            skLineSegment(sketch, "E50.rect.right", {"start": v(0.5, 10) * mm, "end": v(0.5, -10) * mm});
            skPoint(sketch, "E50.rect.middle", {"position": v(0, 0) * mm});
            skLineSegment(sketch, "E51.rect.bottom", {"start": v(7.5, 0.5) * mm, "end": v(-7.5, 0.5) * mm});
            skLineSegment(sketch, "E51.rect.top", {"start": v(7.5, -0.5) * mm, "end": v(-7.5, -0.5) * mm});
            skLineSegment(sketch, "E51.rect.left", {"start": v(7.5, 0.5) * mm, "end": v(7.5, -0.5) * mm});
            skLineSegment(sketch, "E51.rect.right", {"start": v(-7.5, 0.5) * mm, "end": v(-7.5, -0.5) * mm});
            skLineSegment(sketch, "E52", {"start": v(0, 10) * mm, "end": v(-1.77, 8.23) * mm});
            skLineSegment(sketch, "E53", {"start": v(0, 10) * mm, "end": v(1.77, 8.23) * mm});
            skLineSegment(sketch, "E54.0", {"start": v(0, 11.41) * mm, "end": v(-2.47, 8.94) * mm});
            skLineSegment(sketch, "E54.1", {"start": v(0, 11.41) * mm, "end": v(2.47, 8.94) * mm});
            skLineSegment(sketch, "E55.0", {"start": v(-9.47, 13.44) * mm, "end": v(9.47, 13.44) * mm});
            skLineSegment(sketch, "E55.1", {"start": v(-9.47, -13.44) * mm, "end": v(-9.47, 13.44) * mm});
            skLineSegment(sketch, "E55.2", {"start": v(-9.47, -13.44) * mm, "end": v(9.47, -13.44) * mm});
            skLineSegment(sketch, "E55.3", {"start": v(9.47, -13.44) * mm, "end": v(9.47, 13.44) * mm});
            skLineSegment(sketch, "E56", {"start": v(-1.77, 8.23) * mm, "end": v(-2.47, 8.94) * mm});
            skLineSegment(sketch, "E57", {"start": v(1.77, 8.23) * mm, "end": v(2.47, 8.94) * mm});
            skLineSegment(sketch, "E58", {"start": v(7.5, 0) * mm, "end": v(5.73, -1.77) * mm});
            skLineSegment(sketch, "E59", {"start": v(7.5, 0) * mm, "end": v(5.73, 1.77) * mm});
            skLineSegment(sketch, "E60.0", {"start": v(8.91, 0) * mm, "end": v(6.44, 2.47) * mm});
            skLineSegment(sketch, "E60.1", {"start": v(8.91, 0) * mm, "end": v(6.44, -2.47) * mm});
            skLineSegment(sketch, "E61", {"start": v(5.73, 1.77) * mm, "end": v(6.44, 2.47) * mm});
            skLineSegment(sketch, "E62", {"start": v(5.73, -1.77) * mm, "end": v(6.44, -2.47) * mm});
            skLineSegment(sketch, "E63", {"start": v(4.08, 11.35) * mm, "end": v(5.49, 9.94) * mm});
            skLineSegment(sketch, "E64", {"start": v(5.49, 9.94) * mm, "end": v(6.9, 11.35) * mm});
            skLineSegment(sketch, "E65", {"start": v(5.49, 9.94) * mm, "end": v(5.49, 7.44) * mm});
            skLineSegment(sketch, "E66.0", {"start": v(5.49, 10.64) * mm, "end": v(6.55, 11.7) * mm});
            skLineSegment(sketch, "E66.1", {"start": v(4.43, 11.7) * mm, "end": v(5.49, 10.64) * mm});
            skSolve(sketch);
        }
        {
            var Q0;
            Q0=makeQuery(id+"F44.imprint","IMPRINT",FACE,{"disambiguationData":[TD([[makeQuery(id+"F44.imprint","IMPRINT",EDGE,{"derivedFrom":sQuery(id+"F44.wireOp",EDGE,"E54.0")}),1.0]])]});
            var Q1;
            {var subQ1=sQuery(id+"F44.wireOp",EDGE,"E50.rect.left");var subQ3=sQuery(id+"F44.wireOp",EDGE,"E50.rect.bottom");var subQ5=makeQuery(id+"F44.imprint","INTERSECT",VERTEX,{"derivedFrom":[subQ3,subQ1]});Q1=makeQuery(id+"F44.imprint","IMPRINT",FACE,{"disambiguationData":[TD([[makeQuery(id+"F44.imprint","IMPRINT",EDGE,{"disambiguationData":[TD([[subQ5,-1.0]])],"derivedFrom":subQ1}),1.0]])]});}
            var Q2;
            {var subQ0=sQuery(id+"F44.wireOp",EDGE,"E50.rect.right");var subQ3=sQuery(id+"F44.wireOp",EDGE,"E50.rect.bottom");var subQ4=makeQuery(id+"F44.imprint","INTERSECT",VERTEX,{"derivedFrom":[subQ3,subQ0]});Q2=makeQuery(id+"F44.imprint","IMPRINT",FACE,{"disambiguationData":[TD([[makeQuery(id+"F44.imprint","IMPRINT",EDGE,{"disambiguationData":[TD([[subQ4,-1.0]])],"derivedFrom":subQ0}),-1.0]])]});}
            var Q3;
            {var subQ3=sQuery(id+"F44.wireOp",EDGE,"E52");var subQ5=sQuery(id+"F44.wireOp",EDGE,"E50.rect.left");var subQ6=makeQuery(id+"F44.imprint","INTERSECT",VERTEX,{"derivedFrom":[subQ5,subQ3]});Q3=makeQuery(id+"F44.imprint","IMPRINT",FACE,{"disambiguationData":[TD([[makeQuery(id+"F44.imprint","IMPRINT",EDGE,{"disambiguationData":[TD([[subQ6,-1.0]])],"derivedFrom":subQ5}),1.0]])]});}
            var Q4;
            {var subQ3=sQuery(id+"F44.wireOp",EDGE,"E50.rect.left");var subQ5=sQuery(id+"F44.wireOp",EDGE,"E51.rect.bottom");var subQ7=makeQuery(id+"F44.imprint","INTERSECT",VERTEX,{"derivedFrom":[subQ3,subQ5]});Q4=makeQuery(id+"F44.imprint","IMPRINT",FACE,{"disambiguationData":[TD([[makeQuery(id+"F44.imprint","IMPRINT",EDGE,{"disambiguationData":[TD([[subQ7,-1.0]])],"derivedFrom":subQ3}),1.0]])]});}
            var Q5;
            {var subQ1=sQuery(id+"F44.wireOp",EDGE,"E51.rect.bottom");var subQ7=sQuery(id+"F44.wireOp",EDGE,"E50.rect.right");var subQ9=makeQuery(id+"F44.imprint","INTERSECT",VERTEX,{"derivedFrom":[subQ7,subQ1]});Q5=makeQuery(id+"F44.imprint","IMPRINT",FACE,{"disambiguationData":[TD([[makeQuery(id+"F44.imprint","IMPRINT",EDGE,{"disambiguationData":[TD([[subQ9,-1.0]])],"derivedFrom":subQ7}),1.0]])]});}
            var Q6;
            {var subQ1=sQuery(id+"F44.wireOp",EDGE,"E51.rect.bottom");var subQ3=sQuery(id+"F44.wireOp",EDGE,"E51.rect.left");var subQ5=makeQuery(id+"F44.imprint","INTERSECT",VERTEX,{"derivedFrom":[subQ1,subQ3]});Q6=makeQuery(id+"F44.imprint","IMPRINT",FACE,{"disambiguationData":[TD([[makeQuery(id+"F44.imprint","IMPRINT",EDGE,{"disambiguationData":[TD([[subQ5,-1.0]])],"derivedFrom":subQ1}),1.0]])]});}
            var Q7;
            {var subQ1=sQuery(id+"F44.wireOp",EDGE,"E51.rect.top");var subQ3=sQuery(id+"F44.wireOp",EDGE,"E51.rect.left");var subQ5=makeQuery(id+"F44.imprint","INTERSECT",VERTEX,{"derivedFrom":[subQ1,subQ3]});Q7=makeQuery(id+"F44.imprint","IMPRINT",FACE,{"disambiguationData":[TD([[makeQuery(id+"F44.imprint","IMPRINT",EDGE,{"disambiguationData":[TD([[subQ5,-1.0]])],"derivedFrom":subQ1}),-1.0]])]});}
            var Q8;
            Q8=makeQuery(id+"F44.imprint","IMPRINT",FACE,{"disambiguationData":[TD([[makeQuery(id+"F44.imprint","IMPRINT",EDGE,{"derivedFrom":sQuery(id+"F44.wireOp",EDGE,"E60.0")}),1.0]])]});
            extrude(context, id + "F45", {"entities" : qUnion([Q0, Q1, Q2, Q3, Q4, Q5, Q6, Q7, Q8]), "operationType" : NewBodyOperationType.REMOVE, "oppositeDirection" : true, "depth" : 1 * mm});
        }
    });
